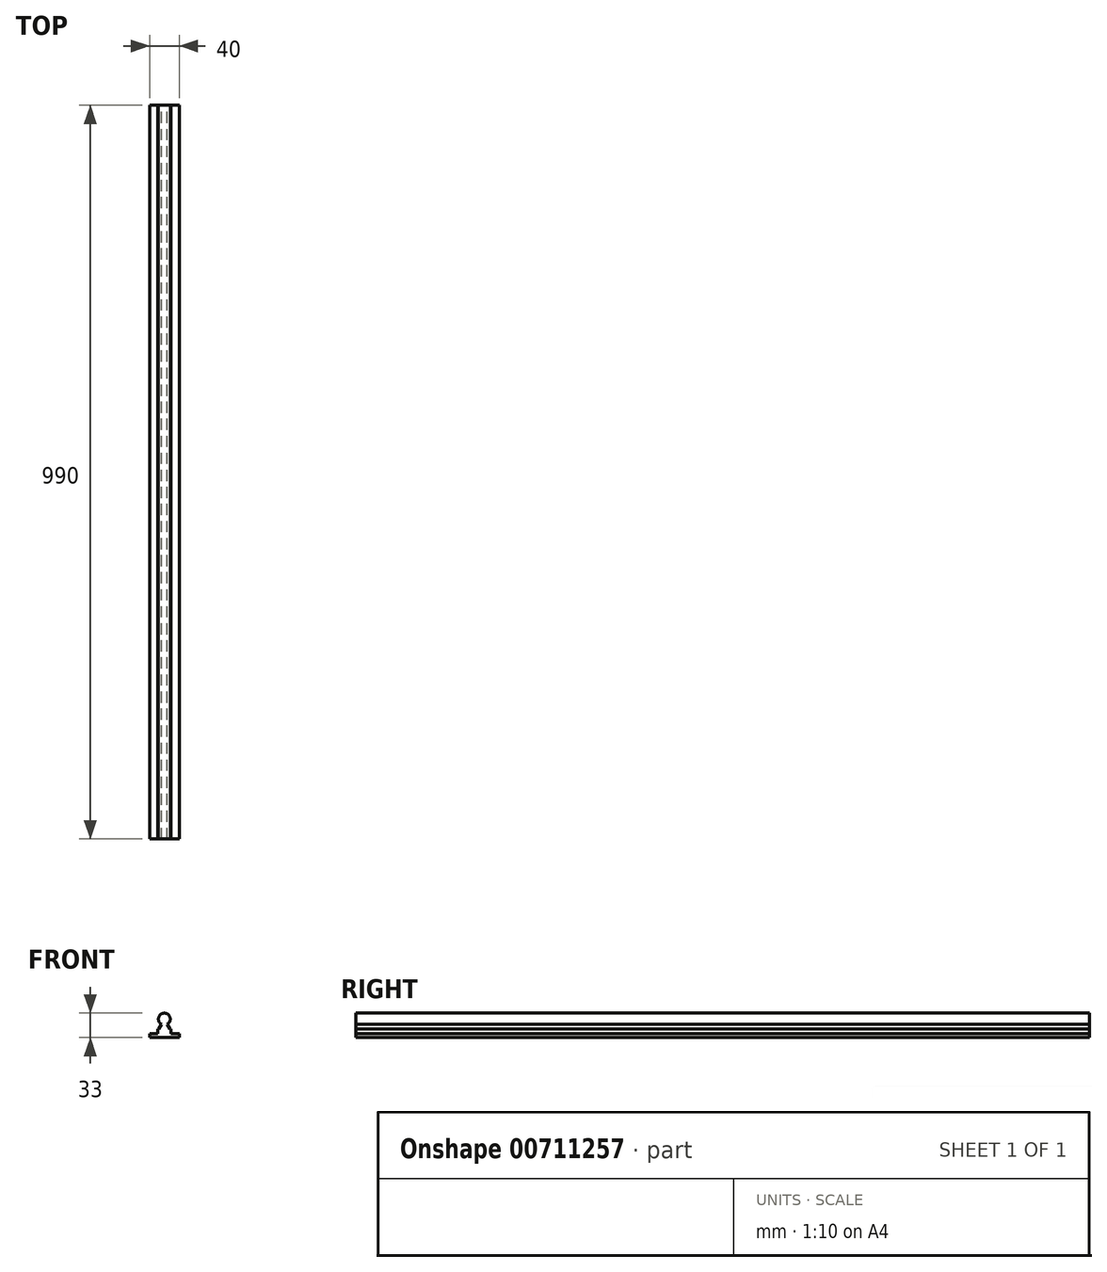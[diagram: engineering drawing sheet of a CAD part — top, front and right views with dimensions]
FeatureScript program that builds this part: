
annotation { "Feature Type Name" : "Feature", "Feature Type Description" : "" }
export const myFeature = defineFeature(function(context is Context, id is Id, definition is map)
    precondition{}
    {
        {
            var Q0;
            Q0=qCreatedBy(makeId("Front.planeOp"),FACE);
            var sketch = newSketch(context, id + "F0", { "sketchPlane" : qUnion([Q0])});
            skLineSegment(sketch, "E0.top", {"start": v(20, -2.5) * mm, "end": v(-20, -2.5) * mm});
            skLineSegment(sketch, "E0.left", {"start": v(20, 2.5) * mm, "end": v(20, -2.5) * mm});
            skLineSegment(sketch, "E0.right", {"start": v(-20, 2.5) * mm, "end": v(-20, -2.5) * mm});
            skPoint(sketch, "E0.middle", {"position": v(0, 0) * mm});
            skArc(sketch, "E1", {"start": v(4, 15.57) * mm, "mid": v(0, 30.5) * mm, "end": v(-4, 15.57) * mm});
            skLineSegment(sketch, "E2", {"start": v(-20, 2.5) * mm, "end": v(-8.9, 2.5) * mm});
            skLineSegment(sketch, "E3", {"start": v(20, 2.5) * mm, "end": v(8.9, 2.5) * mm});
            skLineSegment(sketch, "E4", {"start": v(-8.9, 2.5) * mm, "end": v(-8.9, 9.2) * mm});
            skLineSegment(sketch, "E5", {"start": v(8.9, 2.5) * mm, "end": v(8.9, 9.2) * mm});
            skLineSegment(sketch, "E6", {"start": v(-8.9, 9.2) * mm, "end": v(-7.68, 9.2) * mm});
            skLineSegment(sketch, "E7", {"start": v(8.9, 9.2) * mm, "end": v(7.68, 9.2) * mm});
            skLineSegment(sketch, "E8", {"start": v(-7.68, 9.2) * mm, "end": v(-4, 15.57) * mm});
            skLineSegment(sketch, "E9", {"start": v(7.68, 9.2) * mm, "end": v(4, 15.57) * mm});
            skLineSegment(sketch, "E10.trimOffspring", {"start": v(-8.9, 2.5) * mm, "end": v(-20, 2.5) * mm});
            skSolve(sketch);
        }
        {
            var Q0;
            Q0=makeQuery(id+"F0.imprint","IMPRINT",FACE,{"disambiguationData":[TD([[makeQuery(id+"F0.imprint","IMPRINT",EDGE,{"derivedFrom":sQuery(id+"F0.wireOp",EDGE,"E0.top")}),-1.0]])]});
            extrude(context, id + "F1", {"entities" : qUnion([Q0]), "endBound" : BoundingType.SYMMETRIC, "depth" : 990 * mm, "offsetDistance" : 25 * mm});
        }
    });
